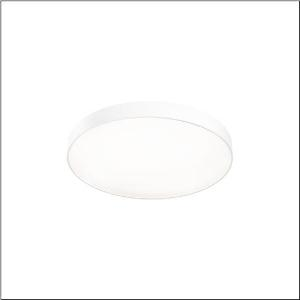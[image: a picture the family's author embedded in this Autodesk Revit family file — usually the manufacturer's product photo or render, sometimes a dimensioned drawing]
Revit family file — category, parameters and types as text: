
# Revit family: round_21_m_51mr36gd0321w
name_source: partatom
category: Lighting Fixtures
units: mm (PartAtom-declared; Revit-internal decimal feet)

## family parameters
Cut with Voids When Loaded = No
Host = Face
Light Source = No
Part Type = Normal
Room Calculation Point = No
Round Connector Dimension = Use Diameter
Shared = No

## types (1)
- Round 21 M (1 x LED, 6840 lm, 54.5 W, 3000K)
    Apparent Load = 55 VA
    CIE Flux Codes = 49 80 96 85 100
    Color Rendering = 80
    Color Temperature = 3000K
    Default Elevation = 1800 mm
    Description = Round 21 M, wall and ceiling luminaire, primary optical cover: cover, of PMMA, opal, light emission: direct/indirect distribution, primary light characteristic: symmetric, installation type: suspended mounting, surface-mounted, LED, rated luminous flux: 6.790lm, luminous efficacy: 124lm/W, light colour: 830, colour temperature: 3000K, with terminal, 5-pole, mains connection: 230V, AC, 50/60Hz, rated input power: 55W, housing, of aluminium, coated, white, diameter: 600mm, height: 62mm, protection rating (complete): IP40, insulation class (complete): insulation class I (protective earthing), certification: CE, impact resistance: IK04, permissible operating ambient temperature: -10..+35°C, packaging unit: 1 piece
    Height = 87 mm
    Lamp = 1 x LED
    Lamp Light Flux = 6840 lm
    Lamp Power = 54.5 W
    Lamp count = 1
    Length = 600 mm
    Luminous efficacy = 126 lm/W
    Manufacturer = Siteco
    ModVariant = No
    Model = 51MR36GD0321W
    Mounting Place = Ceiling
    Mounting Type = Surface mounted
    Number of Poles = 1
    OnlyDefault = Yes
    Power Factor = 1
    Product Name = Round 21 M
    Product group = wall and ceiling luminaire
    ProductGroupID = 302
    Protection Class = Protection class I
    Protection Degree = IP 40
    RLX_Detail_Level = 1
    RLX_Emergency_Light_Flux = 0 lm
    RLX_Emergency_Type = 0
    RLX_Emergency_Type_DB = No
    RlxData = <blob elided: 12097 chars, md5=bcdc47a4>
    Socket = socket
    Standby Power = 0 W
    System Light Flux = 6840 lm
    System Power = 55 W
    Type Comments = Product without accessories
    Type Image = l_1258330.jpg
    URL = http://relux.com
    VarID = ---
    Voltage = 0 V
    Weight = 0.00 kg
    Width = 0 mm  [stored 0 ft]

note: [stored X ft] marks values corroborated as IEEE doubles in the binary element streams (Revit-internal decimal feet)

## geometry (parser evidence)
native form markers: Sweep x11
no freeform markers — native parametric forms only
